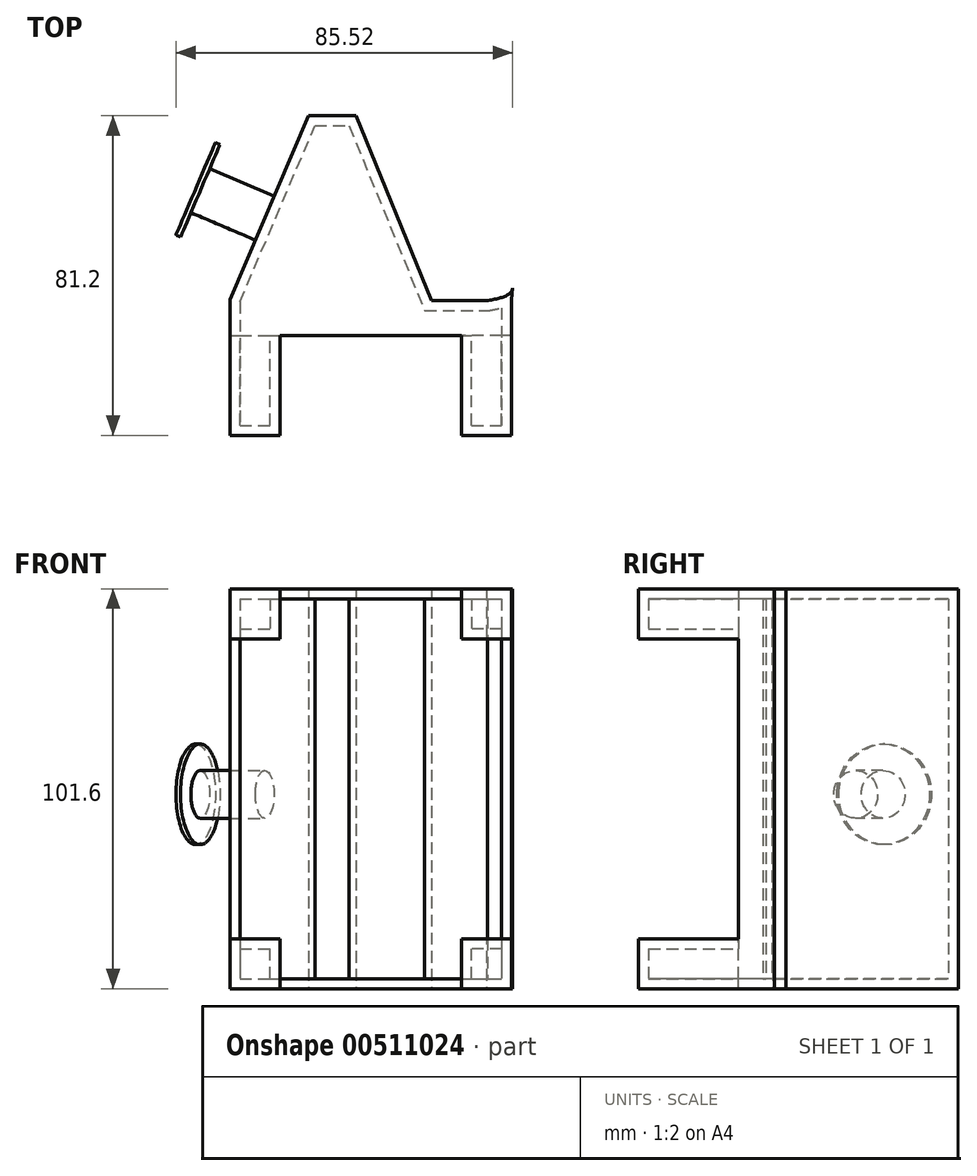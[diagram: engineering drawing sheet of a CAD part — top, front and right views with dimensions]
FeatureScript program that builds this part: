
annotation { "Feature Type Name" : "Feature", "Feature Type Description" : "" }
export const myFeature = defineFeature(function(context is Context, id is Id, definition is map)
    precondition{}
    {
        {
            var Q0;
            Q0=qCreatedBy(makeId("Top.planeOp"),FACE);
            var sketch = newSketch(context, id + "F0", { "sketchPlane" : qUnion([Q0])});
            skLineSegment(sketch, "E0", {"start": v(-51.19, -8.23) * mm, "end": v(-31.3, 38.51) * mm});
            skLineSegment(sketch, "E1", {"start": v(-31.3, 38.51) * mm, "end": v(-19.21, 38.51) * mm});
            skLineSegment(sketch, "E2", {"start": v(-19.21, 38.51) * mm, "end": v(0, -8.52) * mm});
            skLineSegment(sketch, "E3", {"start": v(0, -8.52) * mm, "end": v(14, -8.52) * mm});
            skLineSegment(sketch, "E4", {"start": v(14, -8.52) * mm, "end": v(8.76, 0) * mm});
            skLineSegment(sketch, "E5.top", {"start": v(-51.19, -17.29) * mm, "end": v(20.39, -17.29) * mm});
            skLineSegment(sketch, "E5.left", {"start": v(-51.19, -8.23) * mm, "end": v(-51.19, -17.29) * mm});
            skLineSegment(sketch, "E5.right", {"start": v(20.39, -8.23) * mm, "end": v(20.39, -17.29) * mm});
            skLineSegment(sketch, "E6", {"start": v(20.62, -5.28) * mm, "end": v(20.39, -8.23) * mm});
            skFitSpline(sketch, "E7.trimOffspring", {"points": [v(14, -8.52) * mm, v(20.62, -5.28) * mm, v(14, 2.47) * mm, v(8.76, 0) * mm], "startDerivative": vector(29.56, 5.3) * mm, "endDerivative": vector(-15.95, -15.89) * mm});
            skSolve(sketch);
        }
        {
            var Q0;
            Q0=makeQuery(id+"F0.imprint","IMPRINT",FACE,{"disambiguationData":[TD([[makeQuery(id+"F0.imprint","IMPRINT",EDGE,{"derivedFrom":sQuery(id+"F0.wireOp",EDGE,"E0")}),-1.0]])]});
            extrude(context, id + "F1", {"entities" : qUnion([Q0]), "depth" : 101.6 * mm, "offsetDistance" : 25.4 * mm});
        }
        {
            var Q0;
            Q0=makeQuery(id+"F1.opExtrude","SWEPT_FACE",FACE,{"disambiguationData":[OSD([sQuery(id+"F0.wireOp",EDGE,"E5.top")])]});
            var sketch = newSketch(context, id + "F2", { "sketchPlane" : qUnion([Q0])});
            skLineSegment(sketch, "E8.bottom", {"start": v(-51.19, 0) * mm, "end": v(-38.49, 0) * mm});
            skLineSegment(sketch, "E8.top", {"start": v(-51.19, 12.7) * mm, "end": v(-38.49, 12.7) * mm});
            skLineSegment(sketch, "E8.left", {"start": v(-51.19, 0) * mm, "end": v(-51.19, 12.7) * mm});
            skLineSegment(sketch, "E8.right", {"start": v(-38.49, 0) * mm, "end": v(-38.49, 12.7) * mm});
            skLineSegment(sketch, "E9.bottom", {"start": v(20.39, 0) * mm, "end": v(7.69, 0) * mm});
            skLineSegment(sketch, "E9.top", {"start": v(20.39, 12.7) * mm, "end": v(7.69, 12.7) * mm});
            skLineSegment(sketch, "E9.left", {"start": v(20.39, 0) * mm, "end": v(20.39, 12.7) * mm});
            skLineSegment(sketch, "E9.right", {"start": v(7.69, 0) * mm, "end": v(7.69, 12.7) * mm});
            skLineSegment(sketch, "E10.bottom", {"start": v(-51.19, 101.6) * mm, "end": v(-38.49, 101.6) * mm});
            skLineSegment(sketch, "E10.top", {"start": v(-51.19, 88.9) * mm, "end": v(-38.49, 88.9) * mm});
            skLineSegment(sketch, "E10.left", {"start": v(-51.19, 101.6) * mm, "end": v(-51.19, 88.9) * mm});
            skLineSegment(sketch, "E10.right", {"start": v(-38.49, 101.6) * mm, "end": v(-38.49, 88.9) * mm});
            skLineSegment(sketch, "E11.bottom", {"start": v(20.39, 101.6) * mm, "end": v(7.69, 101.6) * mm});
            skLineSegment(sketch, "E11.top", {"start": v(20.39, 88.9) * mm, "end": v(7.69, 88.9) * mm});
            skLineSegment(sketch, "E11.left", {"start": v(20.39, 101.6) * mm, "end": v(20.39, 88.9) * mm});
            skLineSegment(sketch, "E11.right", {"start": v(7.69, 101.6) * mm, "end": v(7.69, 88.9) * mm});
            skSolve(sketch);
        }
        {
            var Q0;
            Q0 = qSketchRegion(id + "F2", true);
            extrude(context, id + "F3", {"entities" : qUnion([Q0]), "operationType" : NewBodyOperationType.ADD, "depth" : 25.4 * mm, "offsetDistance" : 25.4 * mm});
        }
        {
            var Q0;
            Q0=makeQuery(id+"F1.opExtrude","SWEPT_FACE",FACE,{"disambiguationData":[OSD([sQuery(id+"F0.wireOp",EDGE,"E5.top")])]});
            shell(context, id + "F4", {"entities" : qUnion([Q0]), "thickness" : 2.54 * mm});
        }
        {
            var Q0;
            Q0=makeQuery(id+"F1.opExtrude","SWEPT_FACE",FACE,{"disambiguationData":[OSD([sQuery(id+"F0.wireOp",EDGE,"E0")])]});
            var sketch = newSketch(context, id + "F5", { "sketchPlane" : qUnion([Q0])});
            skCircle(sketch, "E12", {"center": v(5.1, 49.37) * mm, "radius": 6.06 * mm});
            skSolve(sketch);
        }
        {
            var Q0;
            Q0 = qSketchRegion(id + "F5", true);
            extrude(context, id + "F6", {"entities" : qUnion([Q0]), "operationType" : NewBodyOperationType.ADD, "depth" : 17.78 * mm, "offsetDistance" : 25.4 * mm});
        }
        {
            var Q0;
            Q0=makeQuery(id+"F6.opExtrude","CAP_FACE",FACE,{"disambiguationData":[OSD([sQuery(id+"F5.wireOp",EDGE,"E12")])],"isStart":false});
            var sketch = newSketch(context, id + "F7", { "sketchPlane" : qUnion([Q0])});
            skCircle(sketch, "E13", {"center": v(5.1, 49.37) * mm, "radius": 12.78 * mm});
            skSolve(sketch);
        }
        {
            var Q0;
            Q0 = qSketchRegion(id + "F7", true);
            extrude(context, id + "F8", {"entities" : qUnion([Q0]), "operationType" : NewBodyOperationType.ADD, "depth" : 1.27 * mm, "offsetDistance" : 25.4 * mm});
        }
    });
